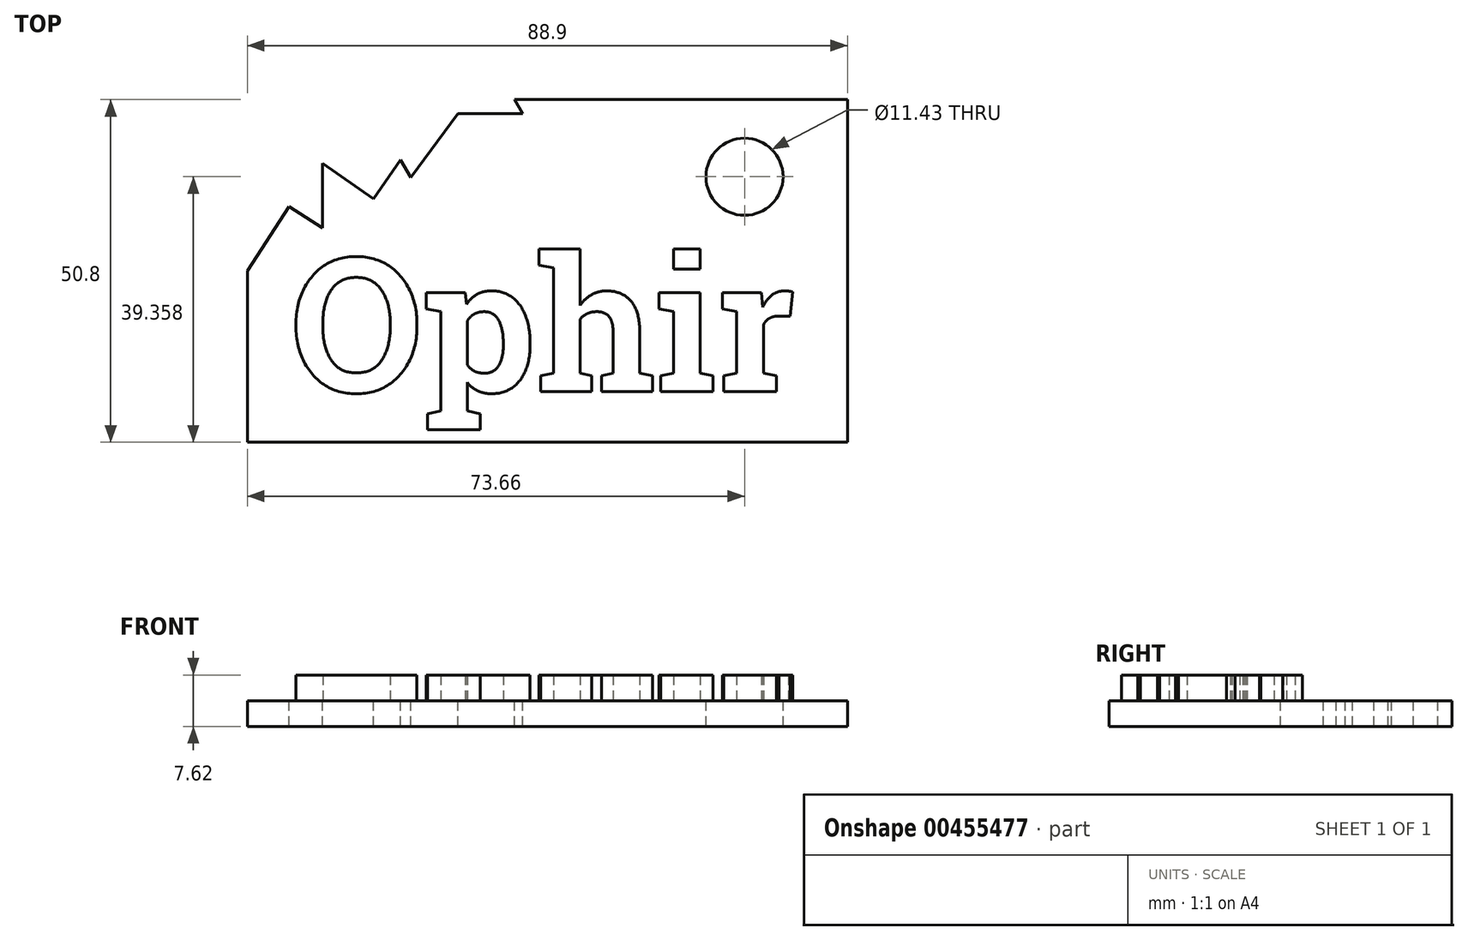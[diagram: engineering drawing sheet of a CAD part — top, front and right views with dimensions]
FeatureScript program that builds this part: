
annotation { "Feature Type Name" : "Feature", "Feature Type Description" : "" }
export const myFeature = defineFeature(function(context is Context, id is Id, definition is map)
    precondition{}
    {
        {
            var Q0;
            Q0=qCreatedBy(makeId("Top.planeOp"),FACE);
            var sketch = newSketch(context, id + "F0", { "sketchPlane" : qUnion([Q0])});
            skLineSegment(sketch, "E0.bottom", {"start": v(44.45, 25.4) * mm, "end": v(-44.45, 25.4) * mm});
            skLineSegment(sketch, "E0.top", {"start": v(44.45, -25.4) * mm, "end": v(-44.45, -25.4) * mm});
            skLineSegment(sketch, "E0.left", {"start": v(44.45, 25.4) * mm, "end": v(44.45, -25.4) * mm});
            skLineSegment(sketch, "E0.right", {"start": v(-44.45, 25.4) * mm, "end": v(-44.45, -25.4) * mm});
            skPoint(sketch, "E0.middle", {"position": v(0, 0) * mm});
            skSolve(sketch);
        }
        {
            var Q0;
            Q0=makeQuery(id+"F0.imprint","IMPRINT",FACE,{"disambiguationData":[TD([[makeQuery(id+"F0.imprint","IMPRINT",EDGE,{"derivedFrom":sQuery(id+"F0.wireOp",EDGE,"E0.bottom")}),1.0]])]});
            extrude(context, id + "F1", {"entities" : qUnion([Q0]), "depth" : 3.8 * mm});
        }
        {
            var Q0;
            Q0=makeQuery(id+"F1.opExtrude","CAP_FACE",FACE,{"disambiguationData":[OSD([sQuery(id+"F0.wireOp",EDGE,"E0.bottom"),sQuery(id+"F0.wireOp",EDGE,"E0.top"),sQuery(id+"F0.wireOp",EDGE,"E0.left"),sQuery(id+"F0.wireOp",EDGE,"E0.right")])],"isStart":false});
            var sketch = newSketch(context, id + "F2", { "sketchPlane" : qUnion([Q0])});
            skText(sketch, "E1", { "text": "Ophir", "fontName": "RobotoSlab-Bold.ttf"});
            skLineSegment(sketch, "E2", {"start": v(-44.45, 25.4) * mm, "end": v(-38.1, 25.4) * mm, "construction": true});
            skLineSegment(sketch, "E3", {"start": v(-38.1, 25.4) * mm, "end": v(-38.1, -25.4) * mm, "construction": true});
            const initialGuessF2  = {"E1": [-0.03814, -0.01792, 1, 0, 0.02002]};
            skSetInitialGuess(sketch, initialGuessF2);
            skSolve(sketch);
        }
        {
            var Q0;
            Q0 = qSketchRegion(id + "F2", true);
            extrude(context, id + "F3", {"entities" : qUnion([Q0]), "operationType" : NewBodyOperationType.ADD, "depth" : 3.8 * mm});
        }
        {
            var Q0;
            {var subQ0=sQuery(id+"F0.wireOp",EDGE,"E0.left");var subQ1=sQuery(id+"F0.wireOp",EDGE,"E0.bottom");var subQ2=sQuery(id+"F0.wireOp",EDGE,"E0.right");var subQ3=sQuery(id+"F0.wireOp",EDGE,"E0.top");Q0=makeQuery(id+"F3.boolean.opBoolean","SPLIT",FACE,{"disambiguationData":[TD([makeQuery(id+"F1.opExtrude","SWEPT_FACE",FACE,{"disambiguationData":[OSD([subQ1])]})])],"derivedFrom":makeQuery(id+"F1.opExtrude","CAP_FACE",FACE,{"disambiguationData":[OSD([subQ1,subQ3,subQ0,subQ2])],"isStart":false})});}
            var sketch = newSketch(context, id + "F4", { "sketchPlane" : qUnion([Q0])});
            skLineSegment(sketch, "E4.bottom", {"start": v(44.45, 25.4) * mm, "end": v(29.21, 25.4) * mm, "construction": true});
            skLineSegment(sketch, "E4.top", {"start": v(44.45, 10.16) * mm, "end": v(29.21, 10.16) * mm, "construction": true});
            skLineSegment(sketch, "E4.left", {"start": v(44.45, 25.4) * mm, "end": v(44.45, 10.16) * mm, "construction": true});
            skLineSegment(sketch, "E4.right", {"start": v(29.21, 25.4) * mm, "end": v(29.21, 10.16) * mm, "construction": true});
            skLineSegment(sketch, "E5", {"start": v(29.21, 10.16) * mm, "end": v(29.21, 13.96) * mm, "construction": true});
            skCircle(sketch, "E6", {"center": v(29.21, 13.96) * mm, "radius": 5.72 * mm});
            skSolve(sketch);
        }
        {
            var Q0;
            Q0=makeQuery(id+"F4.imprint","IMPRINT",FACE,{"disambiguationData":[TD([[makeQuery(id+"F4.imprint","IMPRINT",EDGE,{"derivedFrom":sQuery(id+"F4.wireOp",EDGE,"E6")}),1.0]])]});
            extrude(context, id + "F5", {"entities" : qUnion([Q0]), "operationType" : NewBodyOperationType.REMOVE, "oppositeDirection" : true, "depth" : 25.4 * mm});
        }
        {
            var Q0;
            {var subQ0=sQuery(id+"F0.wireOp",EDGE,"E0.left");var subQ1=sQuery(id+"F0.wireOp",EDGE,"E0.bottom");var subQ2=sQuery(id+"F0.wireOp",EDGE,"E0.right");var subQ3=sQuery(id+"F0.wireOp",EDGE,"E0.top");Q0=makeQuery(id+"F3.boolean.opBoolean","SPLIT",FACE,{"disambiguationData":[TD([makeQuery(id+"F1.opExtrude","SWEPT_FACE",FACE,{"disambiguationData":[OSD([subQ1])]})])],"derivedFrom":makeQuery(id+"F1.opExtrude","CAP_FACE",FACE,{"disambiguationData":[OSD([subQ1,subQ3,subQ0,subQ2])],"isStart":false})});}
            var sketch = newSketch(context, id + "F6", { "sketchPlane" : qUnion([Q0])});
            skLineSegment(sketch, "E7", {"start": v(-44.45, 0) * mm, "end": v(0, 25.4) * mm, "construction": true});
            skLineSegment(sketch, "E8", {"start": v(-44.45, 0) * mm, "end": v(-38.29, 9.57) * mm});
            skLineSegment(sketch, "E9", {"start": v(-38.29, 9.57) * mm, "end": v(-33.3, 6.37) * mm});
            skLineSegment(sketch, "E10", {"start": v(-33.3, 6.37) * mm, "end": v(-33.3, 15.95) * mm});
            skLineSegment(sketch, "E11", {"start": v(-33.3, 15.95) * mm, "end": v(-25.77, 10.67) * mm});
            skLineSegment(sketch, "E12", {"start": v(-25.77, 10.67) * mm, "end": v(-21.72, 16.46) * mm});
            skLineSegment(sketch, "E13", {"start": v(-21.72, 16.46) * mm, "end": v(-20.23, 13.84) * mm});
            skLineSegment(sketch, "E14", {"start": v(-20.23, 13.84) * mm, "end": v(-13.25, 23.32) * mm});
            skLineSegment(sketch, "E15", {"start": v(-13.25, 23.32) * mm, "end": v(-3.65, 23.32) * mm});
            skLineSegment(sketch, "E16", {"start": v(-3.65, 23.32) * mm, "end": v(-4.84, 25.4) * mm});
            skLineSegment(sketch, "E17", {"start": v(-44.45, 0) * mm, "end": v(-44.45, 25.4) * mm});
            skLineSegment(sketch, "E18", {"start": v(-44.45, 25.4) * mm, "end": v(0, 25.4) * mm});
            skSolve(sketch);
        }
        {
            var Q0;
            Q0=makeQuery(id+"F6.imprint","IMPRINT",FACE,{"disambiguationData":[TD([[makeQuery(id+"F6.imprint","IMPRINT",EDGE,{"derivedFrom":sQuery(id+"F6.wireOp",EDGE,"E8")}),1.0]])]});
            extrude(context, id + "F7", {"entities" : qUnion([Q0]), "operationType" : NewBodyOperationType.REMOVE, "oppositeDirection" : true, "depth" : 25.4 * mm});
        }
    });
